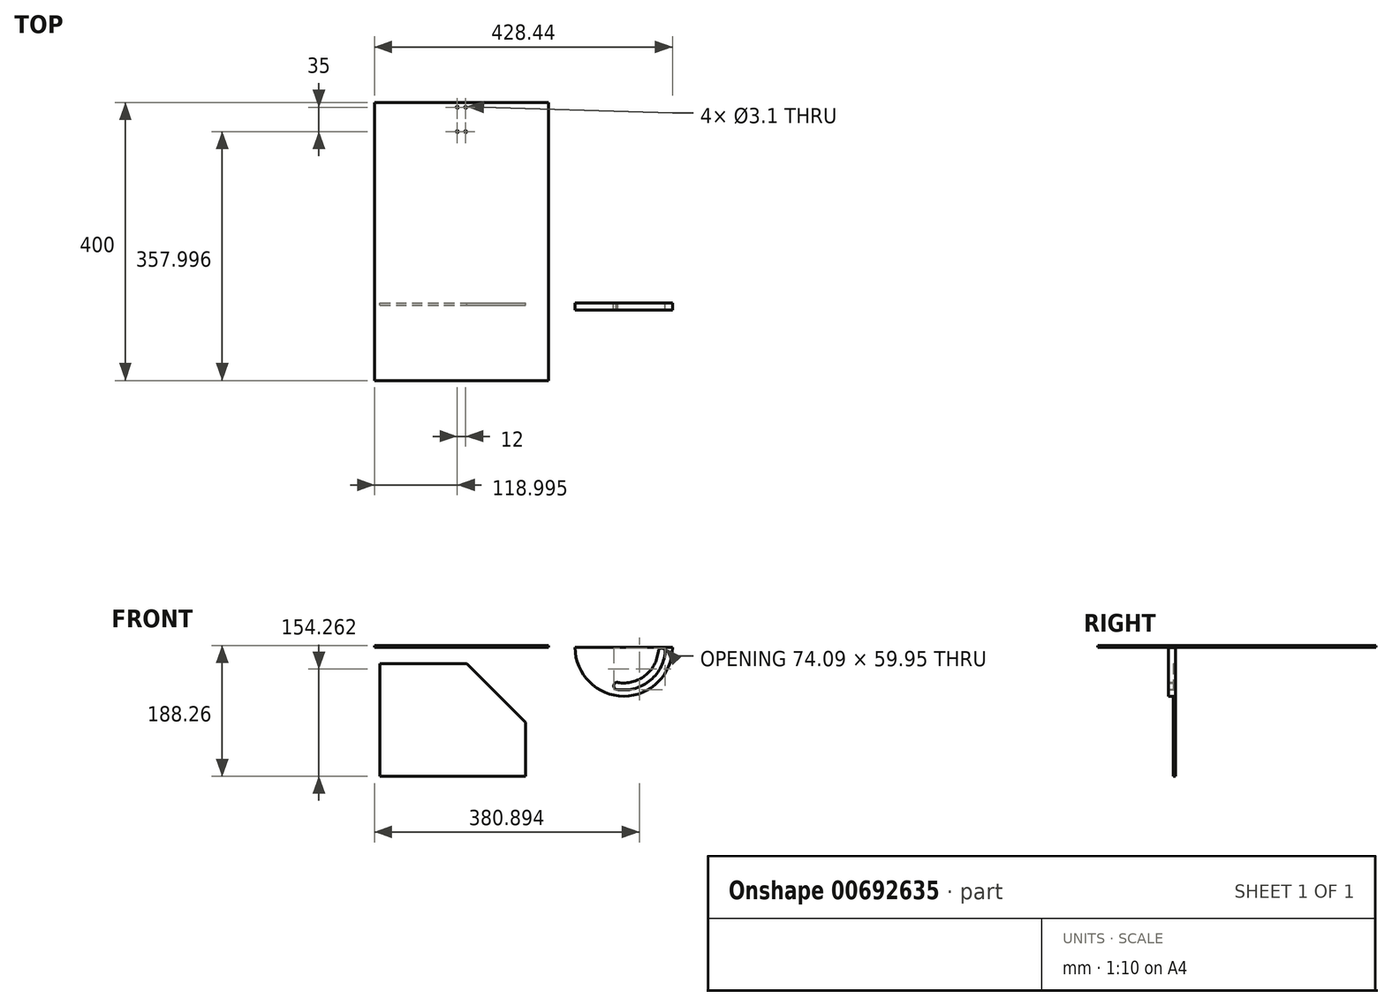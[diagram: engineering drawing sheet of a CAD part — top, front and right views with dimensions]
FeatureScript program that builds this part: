
annotation { "Feature Type Name" : "Feature", "Feature Type Description" : "" }
export const myFeature = defineFeature(function(context is Context, id is Id, definition is map)
    precondition{}
    {
        {
            var Q0;
            Q0=qCreatedBy(makeId("Top.planeOp"),FACE);
            var sketch = newSketch(context, id + "F0", { "sketchPlane" : qUnion([Q0])});
            skLineSegment(sketch, "E0.bottom", {"start": v(-88.66, 288.4) * mm, "end": v(161.34, 288.4) * mm});
            skLineSegment(sketch, "E0.top", {"start": v(-88.66, -111.6) * mm, "end": v(161.34, -111.6) * mm});
            skLineSegment(sketch, "E0.left", {"start": v(-88.66, 288.4) * mm, "end": v(-88.66, -111.6) * mm});
            skLineSegment(sketch, "E0.right", {"start": v(161.34, 288.4) * mm, "end": v(161.34, -111.6) * mm});
            skLineSegment(sketch, "E1", {"start": v(36.34, 288.4) * mm, "end": v(36.34, 163.95) * mm, "construction": true});
            skLineSegment(sketch, "E2.bottom", {"start": v(30.34, 281.4) * mm, "end": v(42.34, 281.4) * mm, "construction": true});
            skLineSegment(sketch, "E2.top", {"start": v(30.34, 246.4) * mm, "end": v(42.34, 246.4) * mm, "construction": true});
            skLineSegment(sketch, "E2.left", {"start": v(30.34, 281.4) * mm, "end": v(30.34, 246.4) * mm, "construction": true});
            skLineSegment(sketch, "E2.right", {"start": v(42.34, 281.4) * mm, "end": v(42.34, 246.4) * mm, "construction": true});
            skCircle(sketch, "E3", {"center": v(30.34, 281.4) * mm, "radius": 1.55 * mm});
            skCircle(sketch, "E4", {"center": v(42.34, 281.4) * mm, "radius": 1.55 * mm});
            skCircle(sketch, "E5", {"center": v(30.34, 246.4) * mm, "radius": 1.55 * mm});
            skCircle(sketch, "E6", {"center": v(42.34, 246.4) * mm, "radius": 1.55 * mm});
            skSolve(sketch);
        }
        {
            var Q0;
            Q0 = qSketchRegion(id + "F0", true);
            extrude(context, id + "F1", {"entities" : qUnion([Q0]), "depth" : 3 * mm, "offsetDistance" : 25 * mm});
        }
        {
            var Q0;
            Q0=qCreatedBy(makeId("Front.planeOp"),FACE);
            var sketch = newSketch(context, id + "F2", { "sketchPlane" : qUnion([Q0])});
            skLineSegment(sketch, "E7.bottom", {"start": v(-80.8, -23.26) * mm, "end": v(44.2, -23.26) * mm});
            skLineSegment(sketch, "E7.top", {"start": v(-80.8, -185.26) * mm, "end": v(128.83, -185.26) * mm});
            skLineSegment(sketch, "E7.left", {"start": v(-80.8, -23.26) * mm, "end": v(-80.8, -185.26) * mm});
            skLineSegment(sketch, "E8", {"start": v(44.2, -23.26) * mm, "end": v(44.2, -185.26) * mm, "construction": true});
            skLineSegment(sketch, "E9", {"start": v(44.2, -23.26) * mm, "end": v(128.83, -107.9) * mm});
            skPoint(sketch, "E7.right.start.orphan", {"position": v(169.2, -23.26) * mm});
            skPoint(sketch, "E10.orphan", {"position": v(169.2, -185.26) * mm});
            skLineSegment(sketch, "E11", {"start": v(128.83, -185.26) * mm, "end": v(128.83, -107.9) * mm});
            skSolve(sketch);
        }
        {
            var Q0;
            Q0 = qSketchRegion(id + "F2", true);
            extrude(context, id + "F3", {"entities" : qUnion([Q0]), "depth" : 3 * mm, "offsetDistance" : 25 * mm});
        }
        {
            var Q0;
            Q0=qCreatedBy(makeId("Front.planeOp"),FACE);
            var sketch = newSketch(context, id + "F4", { "sketchPlane" : qUnion([Q0])});
            skArc(sketch, "E12", {"start": v(199.78, 0) * mm, "mid": v(269.78, -70) * mm, "end": v(339.78, 0) * mm});
            skLineSegment(sketch, "E13", {"start": v(229.53, 0) * mm, "end": v(199.78, 0) * mm});
            skLineSegment(sketch, "E14", {"start": v(199.78, 0) * mm, "end": v(229.53, 0) * mm});
            skLineSegment(sketch, "E15", {"start": v(268.17, -6) * mm, "end": v(339.52, -6) * mm, "construction": true});
            skLineSegment(sketch, "E16", {"start": v(269.78, 0) * mm, "end": v(330.12, -60.34) * mm, "construction": true});
            skLineSegment(sketch, "E17", {"start": v(269.78, 0) * mm, "end": v(251.4, -68.61) * mm, "construction": true});
            skLineSegment(sketch, "E18.trimOffspring", {"start": v(309.53, 0) * mm, "end": v(339.78, 0) * mm});
            skLineSegment(sketch, "E19", {"start": v(261.47, -50.34) * mm, "end": v(258.87, -60.05) * mm, "construction": true});
            skArc(sketch, "E20", {"start": v(261.47, -50.34) * mm, "mid": v(255.32, -53.9) * mm, "end": v(258.87, -60.05) * mm});
            skArc(sketch, "E21.trimOffspring", {"start": v(261.47, -50.34) * mm, "mid": v(300.14, -40.53) * mm, "end": v(319.32, -5.55) * mm});
            skArc(sketch, "E22.trimOffspring", {"start": v(258.87, -60.05) * mm, "mid": v(305.87, -48.74) * mm, "end": v(329.28, -6.45) * mm});
            skArc(sketch, "E23", {"start": v(329.28, -6.45) * mm, "mid": v(324.76, -1.02) * mm, "end": v(319.32, -5.55) * mm});
            skLineSegment(sketch, "E24", {"start": v(229.53, 0) * mm, "end": v(309.53, 0) * mm});
            skSolve(sketch);
        }
        {
            var Q0;
            Q0=makeQuery(id+"F4.imprint","IMPRINT",FACE,{"disambiguationData":[TD([[makeQuery(id+"F4.imprint","IMPRINT",EDGE,{"derivedFrom":sQuery(id+"F4.wireOp",EDGE,"E12")}),1.0]])]});
            extrude(context, id + "F5", {"entities" : qUnion([Q0]), "depth" : 10 * mm, "offsetDistance" : 25 * mm});
        }
    });
